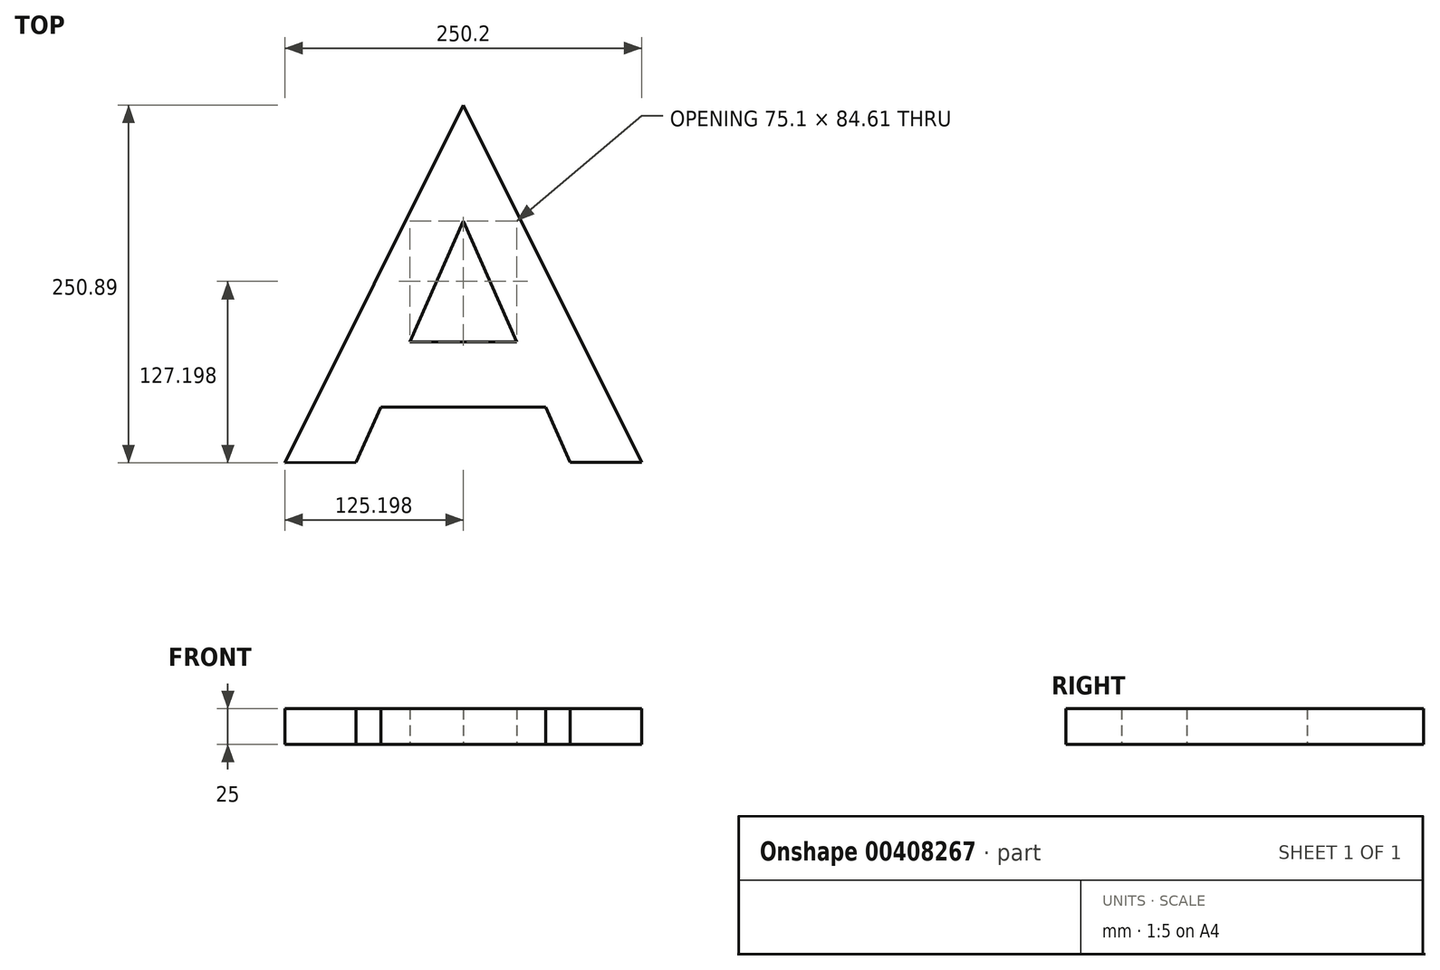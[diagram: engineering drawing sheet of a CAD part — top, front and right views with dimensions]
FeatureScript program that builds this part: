
annotation { "Feature Type Name" : "Feature", "Feature Type Description" : "" }
export const myFeature = defineFeature(function(context is Context, id is Id, definition is map)
    precondition{}
    {
        {
            var Q0;
            Q0=qCreatedBy(makeId("Top.planeOp"),FACE);
            var sketch = newSketch(context, id + "F0", { "sketchPlane" : qUnion([Q0])});
            skLineSegment(sketch, "E0", {"start": v(0, 124.9) * mm, "end": v(-125.3, -126) * mm});
            skLineSegment(sketch, "E1", {"start": v(-125.3, -126) * mm, "end": v(-75.3, -125.7) * mm});
            skLineSegment(sketch, "E2", {"start": v(-75.3, -125.7) * mm, "end": v(0, 43.51) * mm});
            skLineSegment(sketch, "E3", {"start": v(0, 43.51) * mm, "end": v(74.9, -125.7) * mm});
            skLineSegment(sketch, "E4", {"start": v(74.9, -125.7) * mm, "end": v(124.9, -125.7) * mm});
            skLineSegment(sketch, "E5", {"start": v(124.9, -125.7) * mm, "end": v(0, 124.9) * mm});
            skLineSegment(sketch, "E6", {"start": v(-37.65, -41.1) * mm, "end": v(37.45, -41.1) * mm});
            skLineSegment(sketch, "E7", {"start": v(37.45, -41.1) * mm, "end": v(57.69, -86.82) * mm});
            skLineSegment(sketch, "E8", {"start": v(57.69, -86.82) * mm, "end": v(-58, -86.82) * mm});
            skLineSegment(sketch, "E9", {"start": v(-58, -86.82) * mm, "end": v(-37.65, -41.1) * mm});
            skSolve(sketch);
        }
        {
            var Q0;
            Q0 = qSketchRegion(id + "F0", true);
            extrude(context, id + "F1", {"entities" : qUnion([Q0]), "depth" : 25 * mm});
        }
    });
